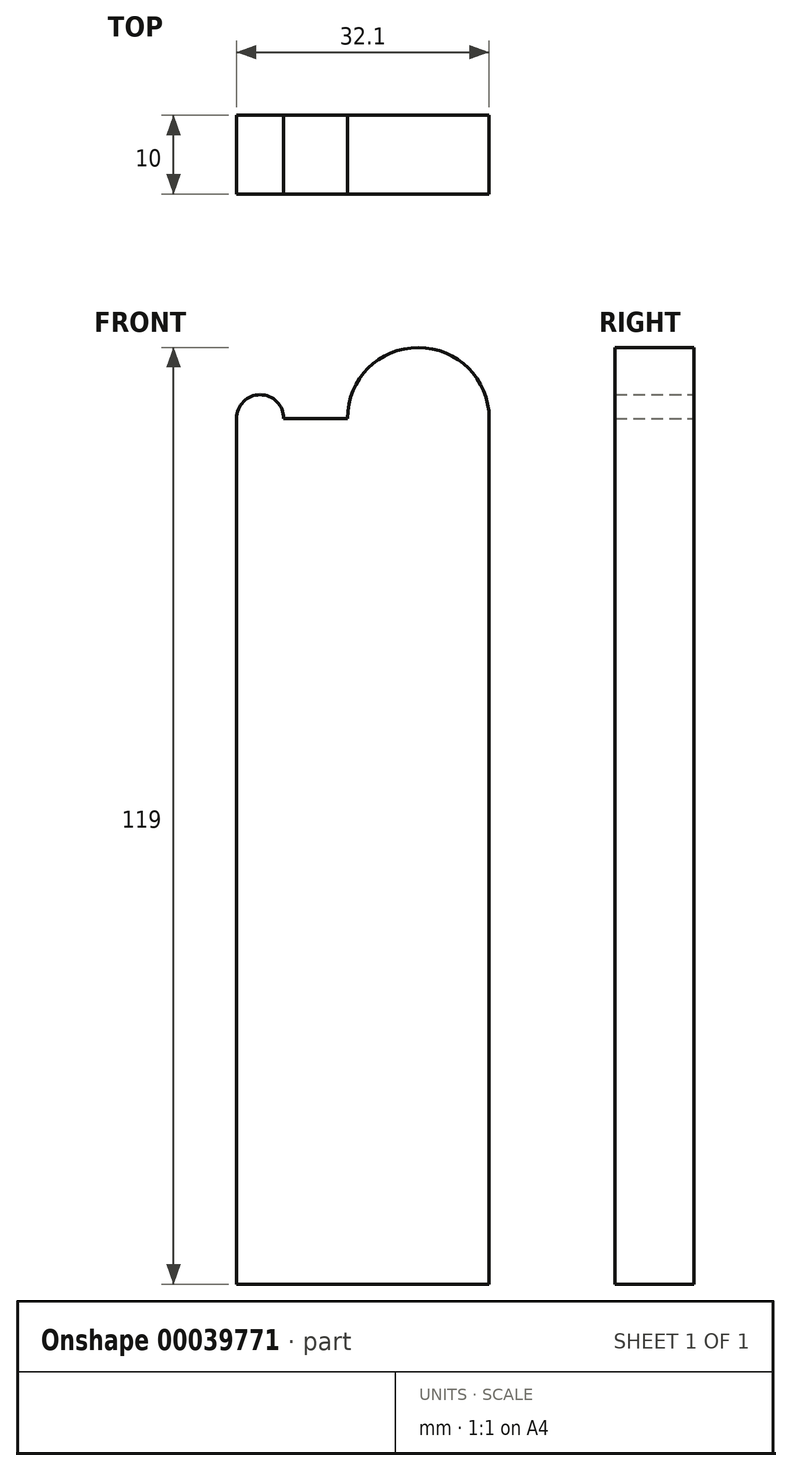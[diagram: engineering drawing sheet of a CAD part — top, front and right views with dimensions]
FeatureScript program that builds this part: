
annotation { "Feature Type Name" : "Feature", "Feature Type Description" : "" }
export const myFeature = defineFeature(function(context is Context, id is Id, definition is map)
    precondition{}
    {
        {
            var Q0;
            Q0=qCreatedBy(makeId("Front.planeOp"),FACE);
            var sketch = newSketch(context, id + "F0", { "sketchPlane" : qUnion([Q0])});
            skLineSegment(sketch, "E0.bottom", {"start": v(-42.54, 48.18) * mm, "end": v(-10.44, 48.18) * mm});
            skLineSegment(sketch, "E0.top", {"start": v(-42.54, -61.82) * mm, "end": v(-10.44, -61.82) * mm});
            skLineSegment(sketch, "E0.left", {"start": v(-42.54, 48.18) * mm, "end": v(-42.54, -61.82) * mm});
            skLineSegment(sketch, "E0.right", {"start": v(-10.44, 48.18) * mm, "end": v(-10.44, -61.82) * mm});
            skArc(sketch, "E1", {"start": v(-10.44, 48.18) * mm, "mid": v(-19.44, 57.18) * mm, "end": v(-28.44, 48.18) * mm});
            skArc(sketch, "E2", {"start": v(-36.54, 48.18) * mm, "mid": v(-39.54, 51.18) * mm, "end": v(-42.54, 48.18) * mm});
            skSolve(sketch);
        }
        {
            var Q0;
            {var subQ0=sQuery(id+"F0.wireOp",EDGE,"E2");Q0=makeQuery(id+"F0.imprint","IMPRINT",FACE,{"disambiguationData":[TD([[makeQuery(id+"F0.imprint","IMPRINT",EDGE,{"derivedFrom":subQ0}),1.0]])]});}
            var Q1;
            {var subQ0=sQuery(id+"F0.wireOp",EDGE,"E1");Q1=makeQuery(id+"F0.imprint","IMPRINT",FACE,{"disambiguationData":[TD([[makeQuery(id+"F0.imprint","IMPRINT",EDGE,{"derivedFrom":subQ0}),1.0]])]});}
            var Q2;
            Q2=makeQuery(id+"F0.imprint","IMPRINT",FACE,{"disambiguationData":[TD([[makeQuery(id+"F0.imprint","IMPRINT",EDGE,{"derivedFrom":sQuery(id+"F0.wireOp",EDGE,"E0.top")}),1.0]])]});
            extrude(context, id + "F1", {"entities" : qUnion([Q0, Q1, Q2]), "depth" : 10 * mm});
        }
    });
